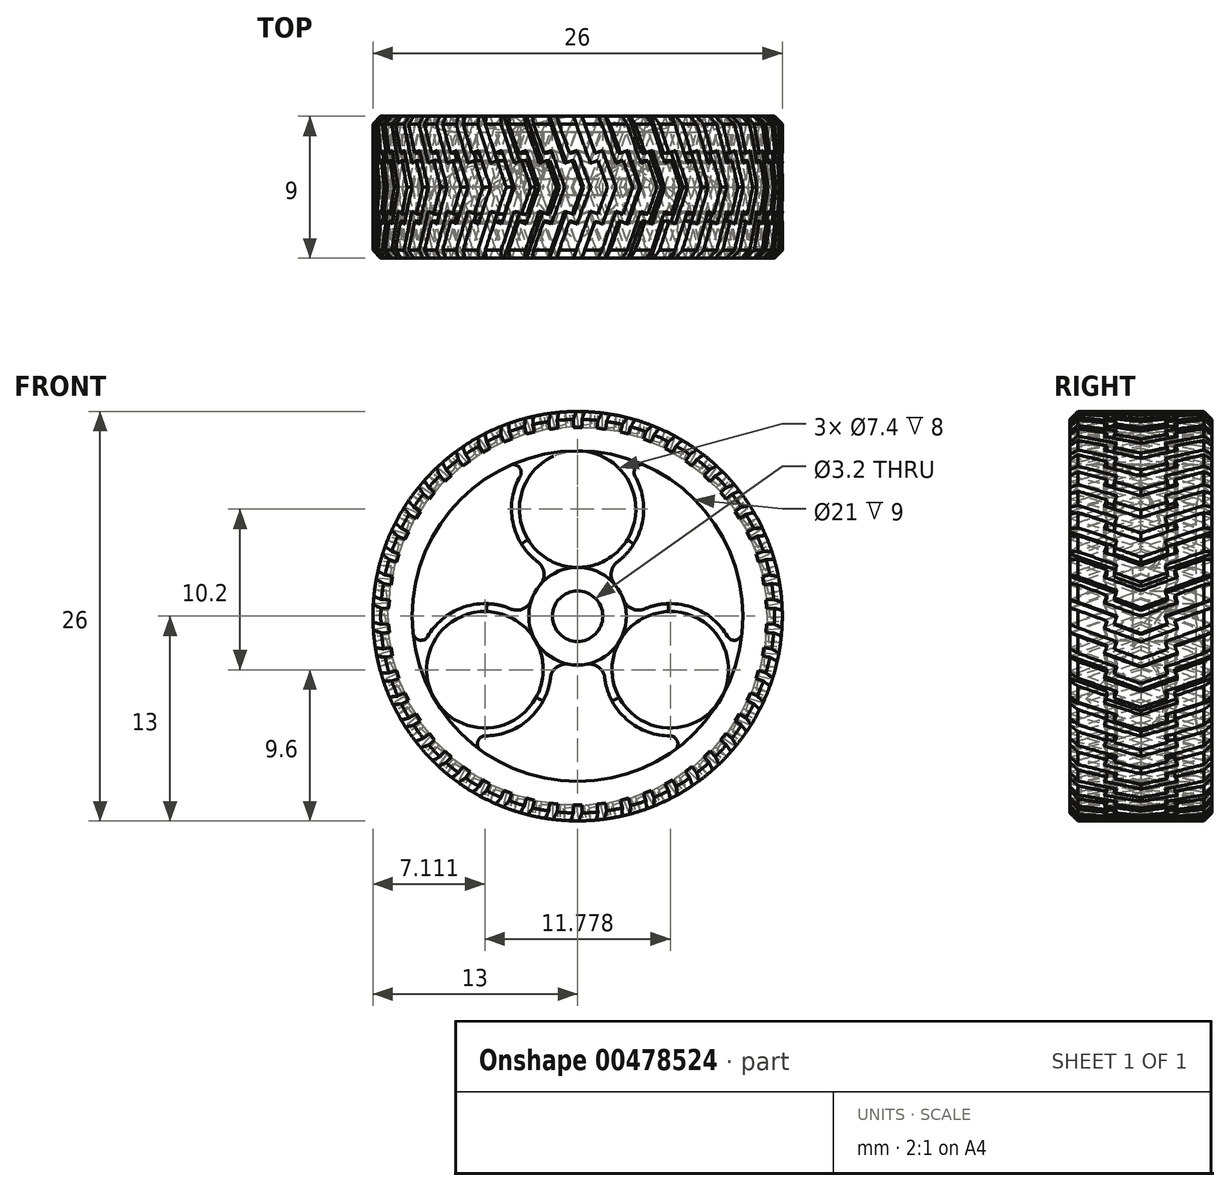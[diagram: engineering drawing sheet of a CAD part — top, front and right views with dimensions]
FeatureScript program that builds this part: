
annotation { "Feature Type Name" : "Feature", "Feature Type Description" : "" }
export const myFeature = defineFeature(function(context is Context, id is Id, definition is map)
    precondition{}
    {
        {
            var Q0;
            Q0=qCreatedBy(makeId("Right.planeOp"),FACE);
            var sketch = newSketch(context, id + "F0", { "sketchPlane" : qUnion([Q0])});
            skLineSegment(sketch, "E0", {"start": v(4.5, 13) * mm, "end": v(4.5, 10.5) * mm});
            skLineSegment(sketch, "E1", {"start": v(4.5, 10.5) * mm, "end": v(-4.5, 10.5) * mm});
            skLineSegment(sketch, "E2", {"start": v(-4.5, 10.5) * mm, "end": v(-4.5, 13) * mm});
            skLineSegment(sketch, "E3", {"start": v(-4.5, 13) * mm, "end": v(4.5, 13) * mm});
            skLineSegment(sketch, "E4", {"start": v(0, 4.58) * mm, "end": v(0, -2.9) * mm, "construction": true});
            skLineSegment(sketch, "E5", {"start": v(3.7, 0) * mm, "end": v(-3.86, 0) * mm, "construction": true});
            skLineSegment(sketch, "E6", {"start": v(3.5, 3.1) * mm, "end": v(3.5, 1.6) * mm});
            skLineSegment(sketch, "E7", {"start": v(3.5, 1.6) * mm, "end": v(1.5, 1.6) * mm});
            skLineSegment(sketch, "E8", {"start": v(1.5, 1.6) * mm, "end": v(1.5, 3.1) * mm});
            skLineSegment(sketch, "E9", {"start": v(1.5, 3.1) * mm, "end": v(3.5, 3.1) * mm});
            skSolve(sketch);
        }
        {
            var Q0;
            Q0=makeQuery(id+"F0.imprint","IMPRINT",FACE,{"disambiguationData":[TD([[makeQuery(id+"F0.imprint","IMPRINT",EDGE,{"derivedFrom":sQuery(id+"F0.wireOp",EDGE,"E0")}),-1.0]])]});
            var Q1;
            Q1=makeQuery(id+"F0.imprint","IMPRINT",FACE,{"disambiguationData":[TD([[makeQuery(id+"F0.imprint","IMPRINT",EDGE,{"derivedFrom":sQuery(id+"F0.wireOp",EDGE,"E6")}),-1.0]])]});
            var Q2;
            Q2=sQuery(id+"F0.wireOp",EDGE,"E5");
            revolve(context, id + "F1", {"entities" : qUnion([Q0, Q1]), "axis" : qUnion([Q2]), "revolveType" : RevolveType.FULL});
        }
        {
            var Q0;
            Q0=makeQuery(id+"F1.opRevolve","SWEPT_FACE",FACE,{"disambiguationData":[OSD([sQuery(id+"F0.wireOp",EDGE,"E6")])]});
            var sketch = newSketch(context, id + "F2", { "sketchPlane" : qUnion([Q0])});
            skCircle(sketch, "E10", {"center": v(0, 6.8) * mm, "radius": 4.2 * mm});
            skCircle(sketch, "E11", {"center": v(0, 6.8) * mm, "radius": 3.7 * mm});
            skLineSegment(sketch, "E12", {"start": v(5.5, 10.5) * mm, "end": v(-6.08, 10.5) * mm, "construction": true});
            skLineSegment(sketch, "E13", {"start": v(-5.55, 11) * mm, "end": v(4.86, 11) * mm, "construction": true});
            skSolve(sketch);
        }
        {
            var Q0;
            {var subQ4=sQuery(id+"F2.wireOp",EDGE,"E11");Q0=makeQuery(id+"F2.imprint","IMPRINT",FACE,{"disambiguationData":[TD([[makeQuery(id+"F2.imprint","IMPRINT",EDGE,{"derivedFrom":subQ4}),-1.0]])]});}
            var Q1;
            {var subQ0=sQuery(id+"F2.wireOp",EDGE,"E10");var subQ1=makeQuery(id+"F1.opRevolve","SWEPT_EDGE",EDGE,{"disambiguationData":[OSD([sQuery(id+"F0.wireOp",EDGE,"E6"),sQuery(id+"F0.wireOp",EDGE,"E9")])]});var subQ2=makeQuery(id+"F2.imprint","INTERSECT",VERTEX,{"disambiguationData":[OD(0.0)],"derivedFrom":[subQ1,subQ0]});Q1=makeQuery(id+"F2.imprint","IMPRINT",FACE,{"disambiguationData":[TD([[makeQuery(id+"F2.imprint","IMPRINT",EDGE,{"disambiguationData":[TD([[subQ2,1.0]])],"derivedFrom":subQ0}),1.0]])]});}
            var Q2;
            Q2=makeQuery(id+"F1.opRevolve","SWEPT_FACE",FACE,{"disambiguationData":[OSD([sQuery(id+"F0.wireOp",EDGE,"E8")])]});
            extrude(context, id + "F3", {"entities" : qUnion([Q0, Q1]), "endBound" : BoundingType.UP_TO_SURFACE, "oppositeDirection" : true, "endBoundEntityFace" : qUnion([Q2]), "depth" : 5 * mm});
        }
        {
            var Q0;
            Q0=makeQuery(id+"F3.opExtrude","SWEPT_BODY",BODY,{"disambiguationData":[OSD([sQuery(id+"F2.wireOp",EDGE,"E10"),sQuery(id+"F2.wireOp",EDGE,"E11")])]});
            var Q1;
            Q1=makeQuery(id+"F1.opRevolve","SWEPT_FACE",FACE,{"disambiguationData":[OSD([sQuery(id+"F0.wireOp",EDGE,"E9")])]});
            circularPattern(context, id + "F4", {"entities" : qUnion([Q0]), "axis" : qUnion([Q1]), "angle" : 360 * degree, "instanceCount" : 3, "equalSpace" : true});
        }
        {
            var Q0;
            Q0=makeQuery(id+"F3.opExtrude","SWEPT_BODY",BODY,{"disambiguationData":[OSD([sQuery(id+"F2.wireOp",EDGE,"E10"),sQuery(id+"F2.wireOp",EDGE,"E11")])]});
            var Q1;
            Q1=makeQuery(id+"F4.opPattern","COPY",BODY,{"derivedFrom":makeQuery(id+"F3.opExtrude","SWEPT_BODY",BODY,{"disambiguationData":[OSD([sQuery(id+"F2.wireOp",EDGE,"E10"),sQuery(id+"F2.wireOp",EDGE,"E11")])]}),"instanceName":"4"});
            var Q2;
            Q2=makeQuery(id+"F4.opPattern","COPY",BODY,{"derivedFrom":makeQuery(id+"F3.opExtrude","SWEPT_BODY",BODY,{"disambiguationData":[OSD([sQuery(id+"F2.wireOp",EDGE,"E10"),sQuery(id+"F2.wireOp",EDGE,"E11")])]}),"instanceName":"3"});
            var Q3;
            Q3=makeQuery(id+"F4.opPattern","COPY",BODY,{"derivedFrom":makeQuery(id+"F3.opExtrude","SWEPT_BODY",BODY,{"disambiguationData":[OSD([sQuery(id+"F2.wireOp",EDGE,"E10"),sQuery(id+"F2.wireOp",EDGE,"E11")])]}),"instanceName":"2"});
            var Q4;
            Q4=makeQuery(id+"F4.opPattern","COPY",BODY,{"derivedFrom":makeQuery(id+"F3.opExtrude","SWEPT_BODY",BODY,{"disambiguationData":[OSD([sQuery(id+"F2.wireOp",EDGE,"E10"),sQuery(id+"F2.wireOp",EDGE,"E11")])]}),"instanceName":"1"});
            var Q5;
            Q5=makeQuery(id+"F1.opRevolve","SWEPT_BODY",BODY,{"disambiguationData":[OSD([sQuery(id+"F0.wireOp",EDGE,"E6"),sQuery(id+"F0.wireOp",EDGE,"E7"),sQuery(id+"F0.wireOp",EDGE,"E8"),sQuery(id+"F0.wireOp",EDGE,"E9")])]});
            booleanBodies(context, id + "F5", {"operationType" : BooleanOperationType.UNION, "tools" : qUnion([Q0, Q1, Q2, Q3, Q4, Q5])});
        }
        {
            var Q0;
            Q0=makeQuery(id+"F3.opExtrude","SWEPT_BODY",BODY,{"disambiguationData":[OSD([sQuery(id+"F2.wireOp",EDGE,"E10"),sQuery(id+"F2.wireOp",EDGE,"E11")])]});
            var Q1;
            Q1=makeQuery(id+"F1.opRevolve","SWEPT_BODY",BODY,{"disambiguationData":[OSD([sQuery(id+"F0.wireOp",EDGE,"E0"),sQuery(id+"F0.wireOp",EDGE,"E1"),sQuery(id+"F0.wireOp",EDGE,"E2"),sQuery(id+"F0.wireOp",EDGE,"E3")])]});
            booleanBodies(context, id + "F6", {"operationType" : BooleanOperationType.UNION, "tools" : qUnion([Q0, Q1])});
        }
        {
            var Q0;
            {var subQ0=sQuery(id+"F0.wireOp",EDGE,"E0");var subQ1=sQuery(id+"F0.wireOp",EDGE,"E3");Q0=makeQuery(id+"F11.boolean.opBoolean","SPLIT",EDGE,{"disambiguationData":[TD([makeQuery(id+"F11.opPattern","COPY",FACE,{"derivedFrom":makeQuery(id+"F10.opExtrude","SWEPT_FACE",FACE,{"disambiguationData":[OSD([sQuery(id+"F9.wireOp",EDGE,"E14")])]}),"instanceName":"47"})])],"derivedFrom":makeQuery(id+"F1.opRevolve","SWEPT_EDGE",EDGE,{"disambiguationData":[OSD([subQ0,subQ1])]})});}
            var Q1;
            Q1=makeQuery(id+"F1.opRevolve","SWEPT_EDGE",EDGE,{"disambiguationData":[OSD([sQuery(id+"F0.wireOp",EDGE,"E2"),sQuery(id+"F0.wireOp",EDGE,"E3")])]});
            chamfer(context, id + "F7", {"entities" : qUnion([Q0, Q1]), "width" : .5 * mm, "tangentPropagation" : true});
        }
        {
            var Q0;
            Q0=qCreatedBy(makeId("Top.planeOp"),FACE);
            cPlane(context, id + "F8", {"entities" : qUnion([Q0]), "cplaneType" : CPlaneType.OFFSET, "offset" : 26 / 2 * mm, "width" : 150 * mm, "height" : 150 * mm});
        }
        {
            var Q0;
            Q0=qCreatedBy(id+"F8.planeOp",FACE);
            var sketch = newSketch(context, id + "F9", { "sketchPlane" : qUnion([Q0])});
            skLineSegment(sketch, "E14", {"start": v(0.27, 4.5) * mm, "end": v(1.12, 2.16) * mm});
            skLineSegment(sketch, "E15", {"start": v(1.59, 2.34) * mm, "end": v(1.12, 2.16) * mm});
            skLineSegment(sketch, "E16", {"start": v(1.59, 2.34) * mm, "end": v(2.44, 0) * mm});
            skLineSegment(sketch, "E17", {"start": v(-13.36, 0) * mm, "end": v(12.93, 0) * mm, "construction": true});
            skLineSegment(sketch, "E18", {"start": v(-0.27, 4.5) * mm, "end": v(0.82, 1.52) * mm});
            skLineSegment(sketch, "E19", {"start": v(0.82, 1.52) * mm, "end": v(1.29, 1.7) * mm});
            skLineSegment(sketch, "E20", {"start": v(1.29, 1.7) * mm, "end": v(1.9, 0) * mm});
            skLineSegment(sketch, "E21", {"start": v(-0.27, 4.5) * mm, "end": v(0.27, 4.5) * mm});
            skPoint(sketch, "E22", {"position": v(0, 4.5) * mm});
            skLineSegment(sketch, "E23.MirrorCS", {"start": v(1.59, -2.34) * mm, "end": v(2.44, 0) * mm});
            skLineSegment(sketch, "E24.MirrorCS", {"start": v(1.29, -1.7) * mm, "end": v(1.9, 0) * mm});
            skLineSegment(sketch, "E25.MirrorCS", {"start": v(0.82, -1.52) * mm, "end": v(1.29, -1.7) * mm});
            skLineSegment(sketch, "E26.MirrorCS", {"start": v(1.59, -2.34) * mm, "end": v(1.12, -2.16) * mm});
            skLineSegment(sketch, "E27.MirrorCS", {"start": v(0.27, -4.5) * mm, "end": v(1.12, -2.16) * mm});
            skLineSegment(sketch, "E28.MirrorCS", {"start": v(-0.27, -4.5) * mm, "end": v(0.82, -1.52) * mm});
            skLineSegment(sketch, "E29.MirrorCS", {"start": v(-0.27, -4.5) * mm, "end": v(0.27, -4.5) * mm});
            skLineSegment(sketch, "E30.0", {"start": v(-12.5, 4.5) * mm, "end": v(12.5, 4.5) * mm});
            skLineSegment(sketch, "E31.0", {"start": v(12.5, -4.5) * mm, "end": v(-12.5, -4.5) * mm});
            skSolve(sketch);
        }
        {
            var Q0;
            Q0=makeQuery(id+"F9.imprint","IMPRINT",FACE,{"disambiguationData":[TD([[makeQuery(id+"F9.imprint","IMPRINT",EDGE,{"derivedFrom":sQuery(id+"F9.wireOp",EDGE,"E14")}),-1.0]])]});
            extrude(context, id + "F10", {"entities" : qUnion([Q0]), "oppositeDirection" : true, "depth" : 1 * mm});
        }
        {
            var Q0;
            Q0=makeQuery(id+"F10.opExtrude","SWEPT_BODY",BODY,{"disambiguationData":[OSD([sQuery(id+"F9.wireOp",EDGE,"E14"),sQuery(id+"F9.wireOp",EDGE,"E15"),sQuery(id+"F9.wireOp",EDGE,"E16"),sQuery(id+"F9.wireOp",EDGE,"E18"),sQuery(id+"F9.wireOp",EDGE,"E19"),sQuery(id+"F9.wireOp",EDGE,"E20"),sQuery(id+"F9.wireOp",EDGE,"E21"),sQuery(id+"F9.wireOp",EDGE,"E23.MirrorCS"),sQuery(id+"F9.wireOp",EDGE,"E24.MirrorCS"),sQuery(id+"F9.wireOp",EDGE,"E25.MirrorCS"),sQuery(id+"F9.wireOp",EDGE,"E26.MirrorCS"),sQuery(id+"F9.wireOp",EDGE,"E27.MirrorCS"),sQuery(id+"F9.wireOp",EDGE,"E28.MirrorCS"),sQuery(id+"F9.wireOp",EDGE,"E29.MirrorCS")])]});
            var Q1;
            Q1=makeQuery(id+"F1.opRevolve","SWEPT_FACE",FACE,{"disambiguationData":[OSD([sQuery(id+"F0.wireOp",EDGE,"E3")])]});
            var Q2;
            Q2=makeQuery(id+"F3.opExtrude","SWEPT_BODY",BODY,{"disambiguationData":[OSD([sQuery(id+"F2.wireOp",EDGE,"E10"),sQuery(id+"F2.wireOp",EDGE,"E11")])]});
            circularPattern(context, id + "F11", {"operationType" : NewBodyOperationType.REMOVE, "entities" : qUnion([Q0]), "axis" : qUnion([Q1]), "angle" : 360 * degree, "instanceCount" : 50, "equalSpace" : true});
        }
        {
            var Q0;
            {var subQ0=sQuery(id+"F0.wireOp",EDGE,"E8");var subQ1=makeQuery(id+"F3.opExtrude","CAP_FACE",FACE,{"disambiguationData":[OSD([subQ0])],"isStart":false});Q0=makeQuery(id+"F5.opBoolean","MERGE",FACE,{"derivedFrom":[makeQuery(id+"F1.opRevolve","SWEPT_FACE",FACE,{"disambiguationData":[OSD([subQ0])]}),subQ1,makeQuery(id+"F4.opPattern","COPY",FACE,{"derivedFrom":subQ1,"instanceName":"1"}),makeQuery(id+"F4.opPattern","COPY",FACE,{"derivedFrom":subQ1,"instanceName":"2"}),makeQuery(id+"F4.opPattern","COPY",FACE,{"derivedFrom":subQ1,"instanceName":"3"}),makeQuery(id+"F4.opPattern","COPY",FACE,{"derivedFrom":subQ1,"instanceName":"4"})]});}
            var sketch = newSketch(context, id + "F12", { "sketchPlane" : qUnion([Q0])});
            skCircle(sketch, "E32", {"center": v(0, 0) * mm, "radius": 1.6 * mm});
            skCircle(sketch, "E33", {"center": v(0, 0) * mm, "radius": 3.1 * mm});
            skSolve(sketch);
        }
        {
            var Q0;
            Q0=makeQuery(id+"F12.imprint","IMPRINT",FACE,{"disambiguationData":[TD([[makeQuery(id+"F12.imprint","IMPRINT",EDGE,{"derivedFrom":sQuery(id+"F12.wireOp",EDGE,"E32")}),1.0]])]});
            extrude(context, id + "F13", {"entities" : qUnion([Q0]), "operationType" : NewBodyOperationType.ADD, "depth" : 1 * mm});
        }
        {
            var Q0;
            Q0=makeQuery(id+"F6.opBoolean","INTERSECT",EDGE,{"disambiguationData":[OD(0.0)],"derivedFrom":[makeQuery(id+"F1.opRevolve","SWEPT_FACE",FACE,{"disambiguationData":[OSD([sQuery(id+"F0.wireOp",EDGE,"E1")])]}),makeQuery(id+"F4.opPattern","COPY",FACE,{"derivedFrom":makeQuery(id+"F3.opExtrude","SWEPT_FACE",FACE,{"disambiguationData":[OSD([sQuery(id+"F2.wireOp",EDGE,"E10")])]}),"instanceName":"2"})]});
            var Q1;
            Q1=makeQuery(id+"F6.opBoolean","INTERSECT",EDGE,{"disambiguationData":[OD(1.0)],"derivedFrom":[makeQuery(id+"F1.opRevolve","SWEPT_FACE",FACE,{"disambiguationData":[OSD([sQuery(id+"F0.wireOp",EDGE,"E1")])]}),makeQuery(id+"F4.opPattern","COPY",FACE,{"derivedFrom":makeQuery(id+"F3.opExtrude","SWEPT_FACE",FACE,{"disambiguationData":[OSD([sQuery(id+"F2.wireOp",EDGE,"E10")])]}),"instanceName":"2"})]});
            var Q2;
            Q2=makeQuery(id+"F6.opBoolean","INTERSECT",EDGE,{"disambiguationData":[OD(1.0)],"derivedFrom":[makeQuery(id+"F1.opRevolve","SWEPT_FACE",FACE,{"disambiguationData":[OSD([sQuery(id+"F0.wireOp",EDGE,"E1")])]}),makeQuery(id+"F4.opPattern","COPY",FACE,{"derivedFrom":makeQuery(id+"F3.opExtrude","SWEPT_FACE",FACE,{"disambiguationData":[OSD([sQuery(id+"F2.wireOp",EDGE,"E10")])]}),"instanceName":"1"})]});
            var Q3;
            Q3=makeQuery(id+"F6.opBoolean","INTERSECT",EDGE,{"disambiguationData":[OD(0.0)],"derivedFrom":[makeQuery(id+"F1.opRevolve","SWEPT_FACE",FACE,{"disambiguationData":[OSD([sQuery(id+"F0.wireOp",EDGE,"E1")])]}),makeQuery(id+"F3.opExtrude","SWEPT_FACE",FACE,{"disambiguationData":[OSD([sQuery(id+"F2.wireOp",EDGE,"E10")])]})]});
            var Q4;
            Q4=makeQuery(id+"F6.opBoolean","INTERSECT",EDGE,{"disambiguationData":[OD(1.0)],"derivedFrom":[makeQuery(id+"F1.opRevolve","SWEPT_FACE",FACE,{"disambiguationData":[OSD([sQuery(id+"F0.wireOp",EDGE,"E1")])]}),makeQuery(id+"F3.opExtrude","SWEPT_FACE",FACE,{"disambiguationData":[OSD([sQuery(id+"F2.wireOp",EDGE,"E10")])]})]});
            var Q5;
            Q5=makeQuery(id+"F6.opBoolean","INTERSECT",EDGE,{"disambiguationData":[OD(0.0)],"derivedFrom":[makeQuery(id+"F1.opRevolve","SWEPT_FACE",FACE,{"disambiguationData":[OSD([sQuery(id+"F0.wireOp",EDGE,"E1")])]}),makeQuery(id+"F4.opPattern","COPY",FACE,{"derivedFrom":makeQuery(id+"F3.opExtrude","SWEPT_FACE",FACE,{"disambiguationData":[OSD([sQuery(id+"F2.wireOp",EDGE,"E10")])]}),"instanceName":"1"})]});
            fillet(context, id + "F14", {"entities" : qUnion([Q0, Q1, Q2, Q3, Q4, Q5]), "radius" : .5 * mm, "tangentPropagation" : true, "allowEdgeOverflow" : false});
        }
        {
            var Q0;
            Q0=makeQuery(id+"F5.opBoolean","INTERSECT",EDGE,{"disambiguationData":[OD(0.0)],"derivedFrom":[makeQuery(id+"F1.opRevolve","SWEPT_FACE",FACE,{"disambiguationData":[OSD([sQuery(id+"F0.wireOp",EDGE,"E9")])]}),makeQuery(id+"F4.opPattern","COPY",FACE,{"derivedFrom":makeQuery(id+"F3.opExtrude","SWEPT_FACE",FACE,{"disambiguationData":[OSD([sQuery(id+"F2.wireOp",EDGE,"E10")])]}),"instanceName":"1"})]});
            var Q1;
            Q1=makeQuery(id+"F5.opBoolean","INTERSECT",EDGE,{"disambiguationData":[OD(1.0)],"derivedFrom":[makeQuery(id+"F1.opRevolve","SWEPT_FACE",FACE,{"disambiguationData":[OSD([sQuery(id+"F0.wireOp",EDGE,"E9")])]}),makeQuery(id+"F4.opPattern","COPY",FACE,{"derivedFrom":makeQuery(id+"F3.opExtrude","SWEPT_FACE",FACE,{"disambiguationData":[OSD([sQuery(id+"F2.wireOp",EDGE,"E10")])]}),"instanceName":"1"})]});
            var Q2;
            Q2=makeQuery(id+"F5.opBoolean","INTERSECT",EDGE,{"disambiguationData":[OD(1.0)],"derivedFrom":[makeQuery(id+"F1.opRevolve","SWEPT_FACE",FACE,{"disambiguationData":[OSD([sQuery(id+"F0.wireOp",EDGE,"E9")])]}),makeQuery(id+"F3.opExtrude","SWEPT_FACE",FACE,{"disambiguationData":[OSD([sQuery(id+"F2.wireOp",EDGE,"E10")])]})]});
            var Q3;
            Q3=makeQuery(id+"F5.opBoolean","INTERSECT",EDGE,{"disambiguationData":[OD(0.0)],"derivedFrom":[makeQuery(id+"F1.opRevolve","SWEPT_FACE",FACE,{"disambiguationData":[OSD([sQuery(id+"F0.wireOp",EDGE,"E9")])]}),makeQuery(id+"F4.opPattern","COPY",FACE,{"derivedFrom":makeQuery(id+"F3.opExtrude","SWEPT_FACE",FACE,{"disambiguationData":[OSD([sQuery(id+"F2.wireOp",EDGE,"E10")])]}),"instanceName":"2"})]});
            var Q4;
            Q4=makeQuery(id+"F5.opBoolean","INTERSECT",EDGE,{"disambiguationData":[OD(1.0)],"derivedFrom":[makeQuery(id+"F1.opRevolve","SWEPT_FACE",FACE,{"disambiguationData":[OSD([sQuery(id+"F0.wireOp",EDGE,"E9")])]}),makeQuery(id+"F4.opPattern","COPY",FACE,{"derivedFrom":makeQuery(id+"F3.opExtrude","SWEPT_FACE",FACE,{"disambiguationData":[OSD([sQuery(id+"F2.wireOp",EDGE,"E10")])]}),"instanceName":"2"})]});
            var Q5;
            Q5=makeQuery(id+"F5.opBoolean","INTERSECT",EDGE,{"disambiguationData":[OD(0.0)],"derivedFrom":[makeQuery(id+"F1.opRevolve","SWEPT_FACE",FACE,{"disambiguationData":[OSD([sQuery(id+"F0.wireOp",EDGE,"E9")])]}),makeQuery(id+"F3.opExtrude","SWEPT_FACE",FACE,{"disambiguationData":[OSD([sQuery(id+"F2.wireOp",EDGE,"E10")])]})]});
            fillet(context, id + "F15", {"entities" : qUnion([Q0, Q1, Q2, Q3, Q4, Q5]), "radius" : 1 * mm, "tangentPropagation" : true, "allowEdgeOverflow" : false});
        }
        {
            var Q0;
            {var subQ0=sQuery(id+"F0.wireOp",EDGE,"E8");var subQ1=makeQuery(id+"F3.opExtrude","CAP_FACE",FACE,{"disambiguationData":[OSD([subQ0])],"isStart":false});var subQ2=sQuery(id+"F12.wireOp",EDGE,"E33");Q0=makeQuery(id+"F13.boolean.opBoolean","SPLIT",EDGE,{"disambiguationData":[TD([makeQuery(id+"F1.opRevolve","SWEPT_FACE",FACE,{"disambiguationData":[OSD([subQ0])]}),makeQuery(id+"F1.opRevolve","SWEPT_FACE",FACE,{"disambiguationData":[OSD([sQuery(id+"F0.wireOp",EDGE,"E9")])]}),subQ1,makeQuery(id+"F4.opPattern","COPY",FACE,{"derivedFrom":subQ1,"instanceName":"1"}),makeQuery(id+"F4.opPattern","COPY",FACE,{"derivedFrom":subQ1,"instanceName":"2"}),makeQuery(id+"F4.opPattern","COPY",FACE,{"derivedFrom":makeQuery(id+"F3.opExtrude","SWEPT_FACE",FACE,{"disambiguationData":[OSD([sQuery(id+"F2.wireOp",EDGE,"E10")])]}),"instanceName":"2"}),makeQuery(id+"F4.opPattern","COPY",FACE,{"derivedFrom":makeQuery(id+"F3.opExtrude","SWEPT_FACE",FACE,{"disambiguationData":[OSD([sQuery(id+"F2.wireOp",EDGE,"E11")])]}),"instanceName":"2"}),makeQuery(id+"F13.opExtrude","SWEPT_FACE",FACE,{"disambiguationData":[OSD([subQ2])]})]),OD(1.0)],"derivedFrom":makeQuery(id+"F13.opExtrude","CAP_EDGE",EDGE,{"disambiguationData":[OSD([subQ2])],"isStart":true})});}
            var Q1;
            {var subQ0=sQuery(id+"F0.wireOp",EDGE,"E8");var subQ1=makeQuery(id+"F3.opExtrude","CAP_FACE",FACE,{"disambiguationData":[OSD([subQ0])],"isStart":false});var subQ2=sQuery(id+"F12.wireOp",EDGE,"E33");Q1=makeQuery(id+"F13.boolean.opBoolean","SPLIT",EDGE,{"disambiguationData":[TD([makeQuery(id+"F1.opRevolve","SWEPT_FACE",FACE,{"disambiguationData":[OSD([subQ0])]}),makeQuery(id+"F1.opRevolve","SWEPT_FACE",FACE,{"disambiguationData":[OSD([sQuery(id+"F0.wireOp",EDGE,"E9")])]}),subQ1,makeQuery(id+"F4.opPattern","COPY",FACE,{"derivedFrom":subQ1,"instanceName":"1"}),makeQuery(id+"F4.opPattern","COPY",FACE,{"derivedFrom":subQ1,"instanceName":"2"}),makeQuery(id+"F4.opPattern","COPY",FACE,{"derivedFrom":makeQuery(id+"F3.opExtrude","SWEPT_FACE",FACE,{"disambiguationData":[OSD([sQuery(id+"F2.wireOp",EDGE,"E10")])]}),"instanceName":"2"}),makeQuery(id+"F4.opPattern","COPY",FACE,{"derivedFrom":makeQuery(id+"F3.opExtrude","SWEPT_FACE",FACE,{"disambiguationData":[OSD([sQuery(id+"F2.wireOp",EDGE,"E11")])]}),"instanceName":"2"}),makeQuery(id+"F13.opExtrude","SWEPT_FACE",FACE,{"disambiguationData":[OSD([subQ2])]})]),OD(0.0)],"derivedFrom":makeQuery(id+"F13.opExtrude","CAP_EDGE",EDGE,{"disambiguationData":[OSD([subQ2])],"isStart":true})});}
            var Q2;
            {var subQ0=sQuery(id+"F0.wireOp",EDGE,"E8");var subQ1=makeQuery(id+"F3.opExtrude","CAP_FACE",FACE,{"disambiguationData":[OSD([subQ0])],"isStart":false});var subQ2=sQuery(id+"F12.wireOp",EDGE,"E33");Q2=makeQuery(id+"F13.boolean.opBoolean","SPLIT",EDGE,{"disambiguationData":[TD([makeQuery(id+"F1.opRevolve","SWEPT_FACE",FACE,{"disambiguationData":[OSD([subQ0])]}),makeQuery(id+"F1.opRevolve","SWEPT_FACE",FACE,{"disambiguationData":[OSD([sQuery(id+"F0.wireOp",EDGE,"E9")])]}),subQ1,makeQuery(id+"F3.opExtrude","SWEPT_FACE",FACE,{"disambiguationData":[OSD([sQuery(id+"F2.wireOp",EDGE,"E10")])]}),makeQuery(id+"F3.opExtrude","SWEPT_FACE",FACE,{"disambiguationData":[OSD([sQuery(id+"F2.wireOp",EDGE,"E11")])]}),makeQuery(id+"F4.opPattern","COPY",FACE,{"derivedFrom":subQ1,"instanceName":"1"}),makeQuery(id+"F4.opPattern","COPY",FACE,{"derivedFrom":subQ1,"instanceName":"2"}),makeQuery(id+"F13.opExtrude","SWEPT_FACE",FACE,{"disambiguationData":[OSD([subQ2])]})]),OD(1.0)],"derivedFrom":makeQuery(id+"F13.opExtrude","CAP_EDGE",EDGE,{"disambiguationData":[OSD([subQ2])],"isStart":true})});}
            var Q3;
            {var subQ0=sQuery(id+"F0.wireOp",EDGE,"E8");var subQ1=makeQuery(id+"F3.opExtrude","CAP_FACE",FACE,{"disambiguationData":[OSD([subQ0])],"isStart":false});var subQ2=sQuery(id+"F12.wireOp",EDGE,"E33");Q3=makeQuery(id+"F13.boolean.opBoolean","SPLIT",EDGE,{"disambiguationData":[TD([makeQuery(id+"F1.opRevolve","SWEPT_FACE",FACE,{"disambiguationData":[OSD([subQ0])]}),makeQuery(id+"F1.opRevolve","SWEPT_FACE",FACE,{"disambiguationData":[OSD([sQuery(id+"F0.wireOp",EDGE,"E9")])]}),subQ1,makeQuery(id+"F3.opExtrude","SWEPT_FACE",FACE,{"disambiguationData":[OSD([sQuery(id+"F2.wireOp",EDGE,"E10")])]}),makeQuery(id+"F3.opExtrude","SWEPT_FACE",FACE,{"disambiguationData":[OSD([sQuery(id+"F2.wireOp",EDGE,"E11")])]}),makeQuery(id+"F4.opPattern","COPY",FACE,{"derivedFrom":subQ1,"instanceName":"1"}),makeQuery(id+"F4.opPattern","COPY",FACE,{"derivedFrom":subQ1,"instanceName":"2"}),makeQuery(id+"F13.opExtrude","SWEPT_FACE",FACE,{"disambiguationData":[OSD([subQ2])]})]),OD(0.0)],"derivedFrom":makeQuery(id+"F13.opExtrude","CAP_EDGE",EDGE,{"disambiguationData":[OSD([subQ2])],"isStart":true})});}
            var Q4;
            {var subQ0=sQuery(id+"F0.wireOp",EDGE,"E8");var subQ1=makeQuery(id+"F3.opExtrude","CAP_FACE",FACE,{"disambiguationData":[OSD([subQ0])],"isStart":false});var subQ2=sQuery(id+"F12.wireOp",EDGE,"E33");Q4=makeQuery(id+"F13.boolean.opBoolean","SPLIT",EDGE,{"disambiguationData":[TD([makeQuery(id+"F1.opRevolve","SWEPT_FACE",FACE,{"disambiguationData":[OSD([subQ0])]}),makeQuery(id+"F1.opRevolve","SWEPT_FACE",FACE,{"disambiguationData":[OSD([sQuery(id+"F0.wireOp",EDGE,"E9")])]}),subQ1,makeQuery(id+"F4.opPattern","COPY",FACE,{"derivedFrom":subQ1,"instanceName":"1"}),makeQuery(id+"F4.opPattern","COPY",FACE,{"derivedFrom":makeQuery(id+"F3.opExtrude","SWEPT_FACE",FACE,{"disambiguationData":[OSD([sQuery(id+"F2.wireOp",EDGE,"E10")])]}),"instanceName":"1"}),makeQuery(id+"F4.opPattern","COPY",FACE,{"derivedFrom":makeQuery(id+"F3.opExtrude","SWEPT_FACE",FACE,{"disambiguationData":[OSD([sQuery(id+"F2.wireOp",EDGE,"E11")])]}),"instanceName":"1"}),makeQuery(id+"F4.opPattern","COPY",FACE,{"derivedFrom":subQ1,"instanceName":"2"}),makeQuery(id+"F13.opExtrude","SWEPT_FACE",FACE,{"disambiguationData":[OSD([subQ2])]})]),OD(0.0)],"derivedFrom":makeQuery(id+"F13.opExtrude","CAP_EDGE",EDGE,{"disambiguationData":[OSD([subQ2])],"isStart":true})});}
            var Q5;
            {var subQ0=sQuery(id+"F0.wireOp",EDGE,"E8");var subQ1=makeQuery(id+"F3.opExtrude","CAP_FACE",FACE,{"disambiguationData":[OSD([subQ0])],"isStart":false});var subQ2=sQuery(id+"F12.wireOp",EDGE,"E33");Q5=makeQuery(id+"F13.boolean.opBoolean","SPLIT",EDGE,{"disambiguationData":[TD([makeQuery(id+"F1.opRevolve","SWEPT_FACE",FACE,{"disambiguationData":[OSD([subQ0])]}),makeQuery(id+"F1.opRevolve","SWEPT_FACE",FACE,{"disambiguationData":[OSD([sQuery(id+"F0.wireOp",EDGE,"E9")])]}),subQ1,makeQuery(id+"F4.opPattern","COPY",FACE,{"derivedFrom":subQ1,"instanceName":"1"}),makeQuery(id+"F4.opPattern","COPY",FACE,{"derivedFrom":makeQuery(id+"F3.opExtrude","SWEPT_FACE",FACE,{"disambiguationData":[OSD([sQuery(id+"F2.wireOp",EDGE,"E10")])]}),"instanceName":"1"}),makeQuery(id+"F4.opPattern","COPY",FACE,{"derivedFrom":makeQuery(id+"F3.opExtrude","SWEPT_FACE",FACE,{"disambiguationData":[OSD([sQuery(id+"F2.wireOp",EDGE,"E11")])]}),"instanceName":"1"}),makeQuery(id+"F4.opPattern","COPY",FACE,{"derivedFrom":subQ1,"instanceName":"2"}),makeQuery(id+"F13.opExtrude","SWEPT_FACE",FACE,{"disambiguationData":[OSD([subQ2])]})]),OD(1.0)],"derivedFrom":makeQuery(id+"F13.opExtrude","CAP_EDGE",EDGE,{"disambiguationData":[OSD([subQ2])],"isStart":true})});}
            var Q6;
            {var subQ0=sQuery(id+"F0.wireOp",EDGE,"E8");var subQ1=makeQuery(id+"F3.opExtrude","CAP_FACE",FACE,{"disambiguationData":[OSD([subQ0])],"isStart":false});Q6=makeQuery(id+"F6.opBoolean","INTERSECT",EDGE,{"disambiguationData":[OD(3.0)],"derivedFrom":[makeQuery(id+"F1.opRevolve","SWEPT_FACE",FACE,{"disambiguationData":[OSD([sQuery(id+"F0.wireOp",EDGE,"E1")])]}),makeQuery(id+"F5.opBoolean","MERGE",FACE,{"derivedFrom":[makeQuery(id+"F1.opRevolve","SWEPT_FACE",FACE,{"disambiguationData":[OSD([subQ0])]}),subQ1,makeQuery(id+"F4.opPattern","COPY",FACE,{"derivedFrom":subQ1,"instanceName":"1"}),makeQuery(id+"F4.opPattern","COPY",FACE,{"derivedFrom":subQ1,"instanceName":"2"})]})]});}
            var Q7;
            {var subQ0=sQuery(id+"F0.wireOp",EDGE,"E8");var subQ1=makeQuery(id+"F3.opExtrude","CAP_FACE",FACE,{"disambiguationData":[OSD([subQ0])],"isStart":false});Q7=makeQuery(id+"F6.opBoolean","INTERSECT",EDGE,{"disambiguationData":[OD(2.0)],"derivedFrom":[makeQuery(id+"F1.opRevolve","SWEPT_FACE",FACE,{"disambiguationData":[OSD([sQuery(id+"F0.wireOp",EDGE,"E1")])]}),makeQuery(id+"F5.opBoolean","MERGE",FACE,{"derivedFrom":[makeQuery(id+"F1.opRevolve","SWEPT_FACE",FACE,{"disambiguationData":[OSD([subQ0])]}),subQ1,makeQuery(id+"F4.opPattern","COPY",FACE,{"derivedFrom":subQ1,"instanceName":"1"}),makeQuery(id+"F4.opPattern","COPY",FACE,{"derivedFrom":subQ1,"instanceName":"2"})]})]});}
            var Q8;
            {var subQ0=sQuery(id+"F0.wireOp",EDGE,"E8");var subQ1=makeQuery(id+"F3.opExtrude","CAP_FACE",FACE,{"disambiguationData":[OSD([subQ0])],"isStart":false});Q8=makeQuery(id+"F6.opBoolean","INTERSECT",EDGE,{"disambiguationData":[OD(4.0)],"derivedFrom":[makeQuery(id+"F1.opRevolve","SWEPT_FACE",FACE,{"disambiguationData":[OSD([sQuery(id+"F0.wireOp",EDGE,"E1")])]}),makeQuery(id+"F5.opBoolean","MERGE",FACE,{"derivedFrom":[makeQuery(id+"F1.opRevolve","SWEPT_FACE",FACE,{"disambiguationData":[OSD([subQ0])]}),subQ1,makeQuery(id+"F4.opPattern","COPY",FACE,{"derivedFrom":subQ1,"instanceName":"1"}),makeQuery(id+"F4.opPattern","COPY",FACE,{"derivedFrom":subQ1,"instanceName":"2"})]})]});}
            var Q9;
            {var subQ0=sQuery(id+"F0.wireOp",EDGE,"E8");var subQ1=makeQuery(id+"F3.opExtrude","CAP_FACE",FACE,{"disambiguationData":[OSD([subQ0])],"isStart":false});Q9=makeQuery(id+"F6.opBoolean","INTERSECT",EDGE,{"disambiguationData":[OD(5.0)],"derivedFrom":[makeQuery(id+"F1.opRevolve","SWEPT_FACE",FACE,{"disambiguationData":[OSD([sQuery(id+"F0.wireOp",EDGE,"E1")])]}),makeQuery(id+"F5.opBoolean","MERGE",FACE,{"derivedFrom":[makeQuery(id+"F1.opRevolve","SWEPT_FACE",FACE,{"disambiguationData":[OSD([subQ0])]}),subQ1,makeQuery(id+"F4.opPattern","COPY",FACE,{"derivedFrom":subQ1,"instanceName":"1"}),makeQuery(id+"F4.opPattern","COPY",FACE,{"derivedFrom":subQ1,"instanceName":"2"})]})]});}
            var Q10;
            {var subQ0=sQuery(id+"F0.wireOp",EDGE,"E8");var subQ1=makeQuery(id+"F3.opExtrude","CAP_FACE",FACE,{"disambiguationData":[OSD([subQ0])],"isStart":false});Q10=makeQuery(id+"F6.opBoolean","INTERSECT",EDGE,{"disambiguationData":[OD(1.0)],"derivedFrom":[makeQuery(id+"F1.opRevolve","SWEPT_FACE",FACE,{"disambiguationData":[OSD([sQuery(id+"F0.wireOp",EDGE,"E1")])]}),makeQuery(id+"F5.opBoolean","MERGE",FACE,{"derivedFrom":[makeQuery(id+"F1.opRevolve","SWEPT_FACE",FACE,{"disambiguationData":[OSD([subQ0])]}),subQ1,makeQuery(id+"F4.opPattern","COPY",FACE,{"derivedFrom":subQ1,"instanceName":"1"}),makeQuery(id+"F4.opPattern","COPY",FACE,{"derivedFrom":subQ1,"instanceName":"2"})]})]});}
            var Q11;
            {var subQ0=sQuery(id+"F0.wireOp",EDGE,"E8");var subQ1=makeQuery(id+"F3.opExtrude","CAP_FACE",FACE,{"disambiguationData":[OSD([subQ0])],"isStart":false});Q11=makeQuery(id+"F6.opBoolean","INTERSECT",EDGE,{"disambiguationData":[OD(0.0)],"derivedFrom":[makeQuery(id+"F1.opRevolve","SWEPT_FACE",FACE,{"disambiguationData":[OSD([sQuery(id+"F0.wireOp",EDGE,"E1")])]}),makeQuery(id+"F5.opBoolean","MERGE",FACE,{"derivedFrom":[makeQuery(id+"F1.opRevolve","SWEPT_FACE",FACE,{"disambiguationData":[OSD([subQ0])]}),subQ1,makeQuery(id+"F4.opPattern","COPY",FACE,{"derivedFrom":subQ1,"instanceName":"1"}),makeQuery(id+"F4.opPattern","COPY",FACE,{"derivedFrom":subQ1,"instanceName":"2"})]})]});}
            fillet(context, id + "F16", {"entities" : qUnion([Q0, Q1, Q2, Q3, Q4, Q5, Q6, Q7, Q8, Q9, Q10, Q11]), "radius" : 5 * mm, "tangentPropagation" : true, "allowEdgeOverflow" : false});
        }
        {
            var Q0;
            {var subQ0=makeQuery(id+"F3.opExtrude","CAP_FACE",FACE,{"disambiguationData":[OSD([sQuery(id+"F2.wireOp",EDGE,"E10"),sQuery(id+"F2.wireOp",EDGE,"E11")])],"isStart":true});Q0=makeQuery(id+"F6.opBoolean","INTERSECT",EDGE,{"disambiguationData":[OD(3.0)],"derivedFrom":[makeQuery(id+"F1.opRevolve","SWEPT_FACE",FACE,{"disambiguationData":[OSD([sQuery(id+"F0.wireOp",EDGE,"E1")])]}),makeQuery(id+"F5.opBoolean","MERGE",FACE,{"derivedFrom":[makeQuery(id+"F1.opRevolve","SWEPT_FACE",FACE,{"disambiguationData":[OSD([sQuery(id+"F0.wireOp",EDGE,"E6")])]}),subQ0,makeQuery(id+"F4.opPattern","COPY",FACE,{"derivedFrom":subQ0,"instanceName":"1"}),makeQuery(id+"F4.opPattern","COPY",FACE,{"derivedFrom":subQ0,"instanceName":"2"})]})]});}
            var Q1;
            {var subQ0=makeQuery(id+"F3.opExtrude","CAP_FACE",FACE,{"disambiguationData":[OSD([sQuery(id+"F2.wireOp",EDGE,"E10"),sQuery(id+"F2.wireOp",EDGE,"E11")])],"isStart":true});Q1=makeQuery(id+"F6.opBoolean","INTERSECT",EDGE,{"disambiguationData":[OD(2.0)],"derivedFrom":[makeQuery(id+"F1.opRevolve","SWEPT_FACE",FACE,{"disambiguationData":[OSD([sQuery(id+"F0.wireOp",EDGE,"E1")])]}),makeQuery(id+"F5.opBoolean","MERGE",FACE,{"derivedFrom":[makeQuery(id+"F1.opRevolve","SWEPT_FACE",FACE,{"disambiguationData":[OSD([sQuery(id+"F0.wireOp",EDGE,"E6")])]}),subQ0,makeQuery(id+"F4.opPattern","COPY",FACE,{"derivedFrom":subQ0,"instanceName":"1"}),makeQuery(id+"F4.opPattern","COPY",FACE,{"derivedFrom":subQ0,"instanceName":"2"})]})]});}
            var Q2;
            {var subQ0=makeQuery(id+"F3.opExtrude","CAP_FACE",FACE,{"disambiguationData":[OSD([sQuery(id+"F2.wireOp",EDGE,"E10"),sQuery(id+"F2.wireOp",EDGE,"E11")])],"isStart":true});Q2=makeQuery(id+"F6.opBoolean","INTERSECT",EDGE,{"disambiguationData":[OD(0.0)],"derivedFrom":[makeQuery(id+"F1.opRevolve","SWEPT_FACE",FACE,{"disambiguationData":[OSD([sQuery(id+"F0.wireOp",EDGE,"E1")])]}),makeQuery(id+"F5.opBoolean","MERGE",FACE,{"derivedFrom":[makeQuery(id+"F1.opRevolve","SWEPT_FACE",FACE,{"disambiguationData":[OSD([sQuery(id+"F0.wireOp",EDGE,"E6")])]}),subQ0,makeQuery(id+"F4.opPattern","COPY",FACE,{"derivedFrom":subQ0,"instanceName":"1"}),makeQuery(id+"F4.opPattern","COPY",FACE,{"derivedFrom":subQ0,"instanceName":"2"})]})]});}
            var Q3;
            {var subQ0=makeQuery(id+"F3.opExtrude","CAP_FACE",FACE,{"disambiguationData":[OSD([sQuery(id+"F2.wireOp",EDGE,"E10"),sQuery(id+"F2.wireOp",EDGE,"E11")])],"isStart":true});Q3=makeQuery(id+"F6.opBoolean","INTERSECT",EDGE,{"disambiguationData":[OD(1.0)],"derivedFrom":[makeQuery(id+"F1.opRevolve","SWEPT_FACE",FACE,{"disambiguationData":[OSD([sQuery(id+"F0.wireOp",EDGE,"E1")])]}),makeQuery(id+"F5.opBoolean","MERGE",FACE,{"derivedFrom":[makeQuery(id+"F1.opRevolve","SWEPT_FACE",FACE,{"disambiguationData":[OSD([sQuery(id+"F0.wireOp",EDGE,"E6")])]}),subQ0,makeQuery(id+"F4.opPattern","COPY",FACE,{"derivedFrom":subQ0,"instanceName":"1"}),makeQuery(id+"F4.opPattern","COPY",FACE,{"derivedFrom":subQ0,"instanceName":"2"})]})]});}
            var Q4;
            {var subQ0=makeQuery(id+"F3.opExtrude","CAP_FACE",FACE,{"disambiguationData":[OSD([sQuery(id+"F2.wireOp",EDGE,"E10"),sQuery(id+"F2.wireOp",EDGE,"E11")])],"isStart":true});Q4=makeQuery(id+"F6.opBoolean","INTERSECT",EDGE,{"disambiguationData":[OD(4.0)],"derivedFrom":[makeQuery(id+"F1.opRevolve","SWEPT_FACE",FACE,{"disambiguationData":[OSD([sQuery(id+"F0.wireOp",EDGE,"E1")])]}),makeQuery(id+"F5.opBoolean","MERGE",FACE,{"derivedFrom":[makeQuery(id+"F1.opRevolve","SWEPT_FACE",FACE,{"disambiguationData":[OSD([sQuery(id+"F0.wireOp",EDGE,"E6")])]}),subQ0,makeQuery(id+"F4.opPattern","COPY",FACE,{"derivedFrom":subQ0,"instanceName":"1"}),makeQuery(id+"F4.opPattern","COPY",FACE,{"derivedFrom":subQ0,"instanceName":"2"})]})]});}
            var Q5;
            {var subQ0=makeQuery(id+"F3.opExtrude","CAP_FACE",FACE,{"disambiguationData":[OSD([sQuery(id+"F2.wireOp",EDGE,"E10"),sQuery(id+"F2.wireOp",EDGE,"E11")])],"isStart":true});Q5=makeQuery(id+"F6.opBoolean","INTERSECT",EDGE,{"disambiguationData":[OD(5.0)],"derivedFrom":[makeQuery(id+"F1.opRevolve","SWEPT_FACE",FACE,{"disambiguationData":[OSD([sQuery(id+"F0.wireOp",EDGE,"E1")])]}),makeQuery(id+"F5.opBoolean","MERGE",FACE,{"derivedFrom":[makeQuery(id+"F1.opRevolve","SWEPT_FACE",FACE,{"disambiguationData":[OSD([sQuery(id+"F0.wireOp",EDGE,"E6")])]}),subQ0,makeQuery(id+"F4.opPattern","COPY",FACE,{"derivedFrom":subQ0,"instanceName":"1"}),makeQuery(id+"F4.opPattern","COPY",FACE,{"derivedFrom":subQ0,"instanceName":"2"})]})]});}
            fillet(context, id + "F17", {"entities" : qUnion([Q0, Q1, Q2, Q3, Q4, Q5]), "radius" : 5 * mm, "tangentPropagation" : true, "allowEdgeOverflow" : false});
        }
        {
            var Q0;
            Q0=makeQuery(id+"F13.opExtrude","CAP_FACE",FACE,{"disambiguationData":[OSD([sQuery(id+"F12.wireOp",EDGE,"E32"),sQuery(id+"F12.wireOp",EDGE,"E33")])],"isStart":false});
            extrude(context, id + "F18", {"entities" : qUnion([Q0]), "operationType" : NewBodyOperationType.ADD, "depth" : 1 * mm});
        }
    });
